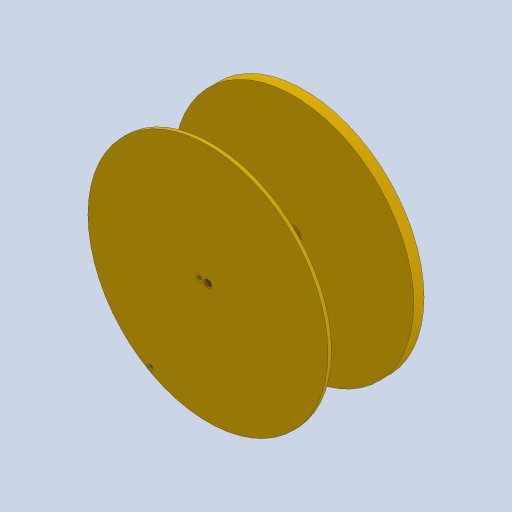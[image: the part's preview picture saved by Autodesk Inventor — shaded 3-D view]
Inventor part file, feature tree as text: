
AUTODESK INVENTOR PART (.ipt)
format: ipt  version: 2024 (Build 280153000, 153)  size: 302,080 bytes
history: native  units: in
note: dims shown in document units (in); Inventor stores cm internally (conversion verified against a paired STEP export)
features: extrude x5, other x2, sketch x1, chamfer x1, hole x1, loft x1
ambient origin geometry x8: Origin, YZ Plane, XZ Plane, XY Plane, X Axis, Y Axis, Z Axis, Center Point
bodies: Solid1 (feature_tree), Solid2 (feature_tree)
feature tree (11):
  extrude  "Extrusion1"  Depth=0.1181in TaperAngle=0.0deg
  extrude  "Extrusion2"  Depth=0.1063in
  extrude  "Extrusion3"  Depth=0.9449in TaperAngle=0.0deg
  extrude  "Extrusion4"  Depth=0.1063in
  sketch  "Sketch6"  dims[d0=2.7559in d1=0.1181in d2=0.0in d3=0.1575in d4=0.9449in d5=0.0in d6=2.7559in d7=0.0394in d8=0.0in d9=0.0866in d10=0.2028in d11=0.0in d20=0.0315in d21=0.0315in d22=0.0591in d23=0.0in d24=0.0157in d25=0.0787in d26=45.0deg d32=0.0984in d34=0.0968in d35=0.2362in d36=0.1575in d37=0.0787in d38=90.0deg d39=0.1063in d40=0.0in d41=1.1614in d44=0.2402in d45=0.9488in d46=0.2756in d47=0.2756in d48=0.1969in d49=0.1969in d50=0.0in d51=90.0deg d52=0.0in d53=90.0deg]
  extrude  "Extrusion5"  Depth=0.0394in TaperAngle=0.0deg
  chamfer  "Chamfer1"  Distance=0.0866in
  hole  "Hole2"  [1 undecoded]
  loft  "Loft1"
  other  "Edges1"
  other  "Edges2"
note: 1 required parameter value undecoded (feature->parameter linkage not recoverable at this tier; creation-order binding heuristic only, values carry confidence <= 0.55)
